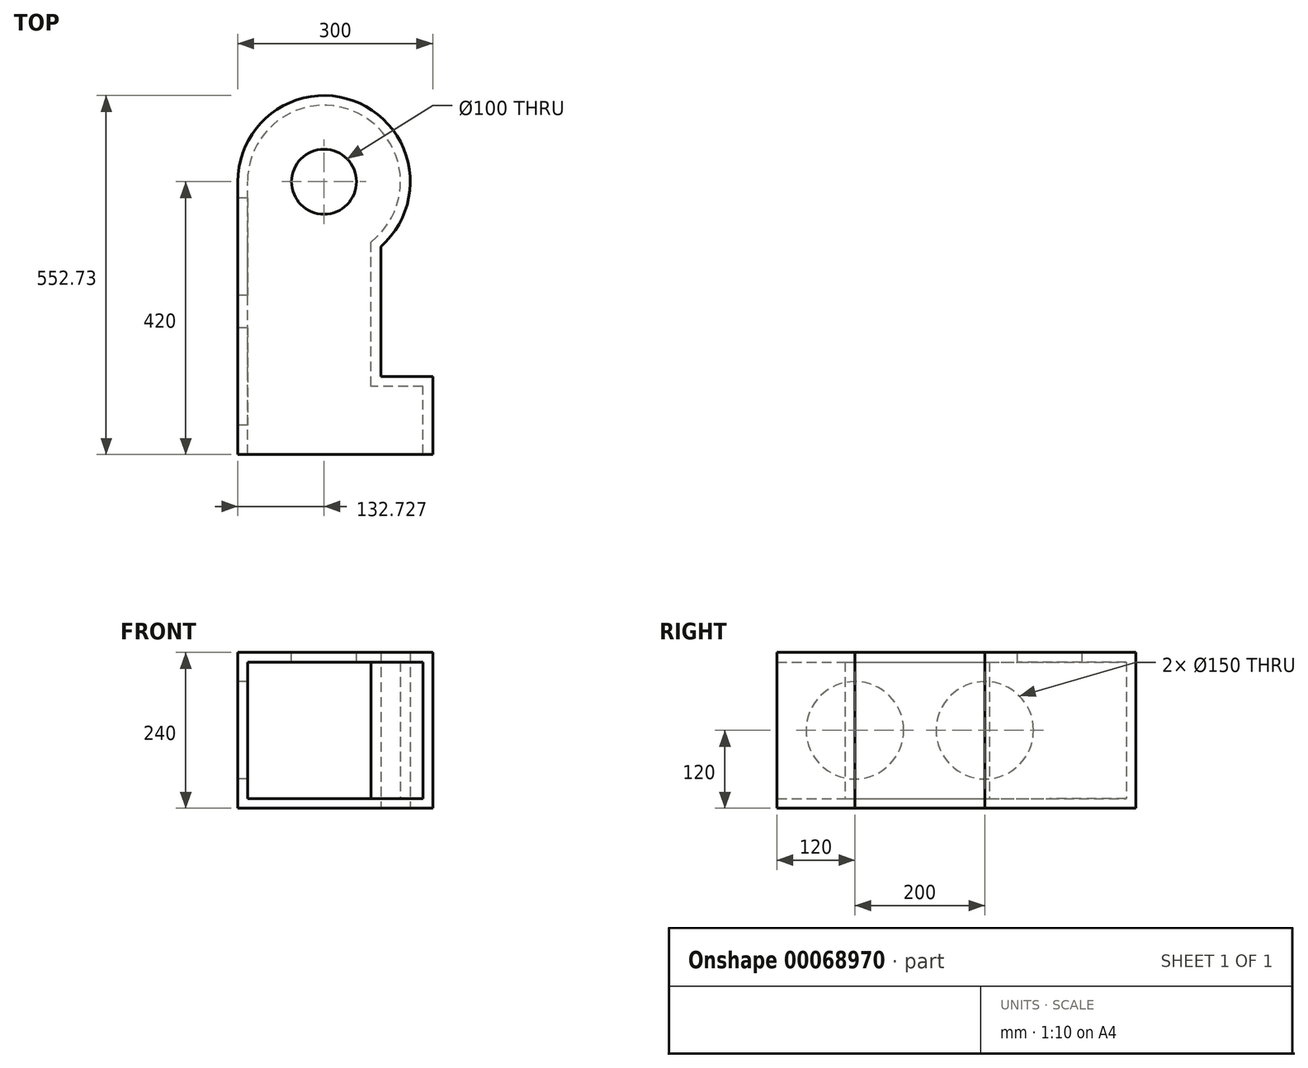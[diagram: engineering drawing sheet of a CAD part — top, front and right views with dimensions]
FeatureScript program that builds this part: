
annotation { "Feature Type Name" : "Feature", "Feature Type Description" : "" }
export const myFeature = defineFeature(function(context is Context, id is Id, definition is map)
    precondition{}
    {
        {
            var Q0;
            Q0=qCreatedBy(makeId("Top.planeOp"),FACE);
            var sketch = newSketch(context, id + "F0", { "sketchPlane" : qUnion([Q0])});
            skLineSegment(sketch, "E0", {"start": v(0, 0) * mm, "end": v(0, 420) * mm});
            skLineSegment(sketch, "E1", {"start": v(0, 0) * mm, "end": v(300, 0) * mm});
            skLineSegment(sketch, "E2", {"start": v(300, 0) * mm, "end": v(300, 120) * mm});
            skLineSegment(sketch, "E3", {"start": v(300, 120) * mm, "end": v(220, 120) * mm});
            skLineSegment(sketch, "E4", {"start": v(220, 120) * mm, "end": v(220, 320) * mm});
            skArc(sketch, "E5", {"start": v(220, 320) * mm, "mid": v(187.65, 540.83) * mm, "end": v(0, 420) * mm});
            skSolve(sketch);
        }
        {
            var Q0;
            Q0=makeQuery(id+"F0.imprint","IMPRINT",FACE,{"disambiguationData":[TD([[makeQuery(id+"F0.imprint","IMPRINT",EDGE,{"derivedFrom":sQuery(id+"F0.wireOp",EDGE,"E0")}),-1.0]])]});
            extrude(context, id + "F1", {"entities" : qUnion([Q0]), "depth" : 240 * mm});
        }
        {
            var Q0;
            Q0=makeQuery(id+"F1.opExtrude","SWEPT_FACE",FACE,{"disambiguationData":[OSD([sQuery(id+"F0.wireOp",EDGE,"E1")])]});
            shell(context, id + "F2", {"entities" : qUnion([Q0]), "thickness" : 15 * mm});
        }
        {
            var Q0;
            Q0=makeQuery(id+"F1.opExtrude","CAP_FACE",FACE,{"disambiguationData":[OSD([sQuery(id+"F0.wireOp",EDGE,"E0"),sQuery(id+"F0.wireOp",EDGE,"E1"),sQuery(id+"F0.wireOp",EDGE,"E2"),sQuery(id+"F0.wireOp",EDGE,"E3"),sQuery(id+"F0.wireOp",EDGE,"E4"),sQuery(id+"F0.wireOp",EDGE,"E5")])],"isStart":false});
            var sketch = newSketch(context, id + "F3", { "sketchPlane" : qUnion([Q0])});
            skCircle(sketch, "E6", {"center": v(132.73, 420) * mm, "radius": 50 * mm});
            skSolve(sketch);
        }
        {
            var Q0;
            Q0=makeQuery(id+"F3.imprint","IMPRINT",FACE,{"disambiguationData":[TD([[makeQuery(id+"F3.imprint","IMPRINT",EDGE,{"derivedFrom":sQuery(id+"F3.wireOp",EDGE,"E6")}),1.0]])]});
            extrude(context, id + "F4", {"entities" : qUnion([Q0]), "operationType" : NewBodyOperationType.REMOVE, "oppositeDirection" : true, "depth" : 50 * mm});
        }
        {
            var Q0;
            Q0=makeQuery(id+"F1.opExtrude","SWEPT_FACE",FACE,{"disambiguationData":[OSD([sQuery(id+"F0.wireOp",EDGE,"E0")])]});
            var sketch = newSketch(context, id + "F5", { "sketchPlane" : qUnion([Q0])});
            skCircle(sketch, "E7", {"center": v(-320, 120) * mm, "radius": 75 * mm});
            skCircle(sketch, "E8", {"center": v(-120, 120) * mm, "radius": 75 * mm});
            skSolve(sketch);
        }
        {
            var Q0;
            Q0=makeQuery(id+"F5.imprint","IMPRINT",FACE,{"disambiguationData":[TD([[makeQuery(id+"F5.imprint","IMPRINT",EDGE,{"derivedFrom":sQuery(id+"F5.wireOp",EDGE,"E7")}),1.0]])]});
            var Q1;
            Q1=makeQuery(id+"F5.imprint","IMPRINT",FACE,{"disambiguationData":[TD([[makeQuery(id+"F5.imprint","IMPRINT",EDGE,{"derivedFrom":sQuery(id+"F5.wireOp",EDGE,"E8")}),1.0]])]});
            extrude(context, id + "F6", {"entities" : qUnion([Q0, Q1]), "operationType" : NewBodyOperationType.REMOVE, "oppositeDirection" : true, "depth" : 50 * mm});
        }
    });
